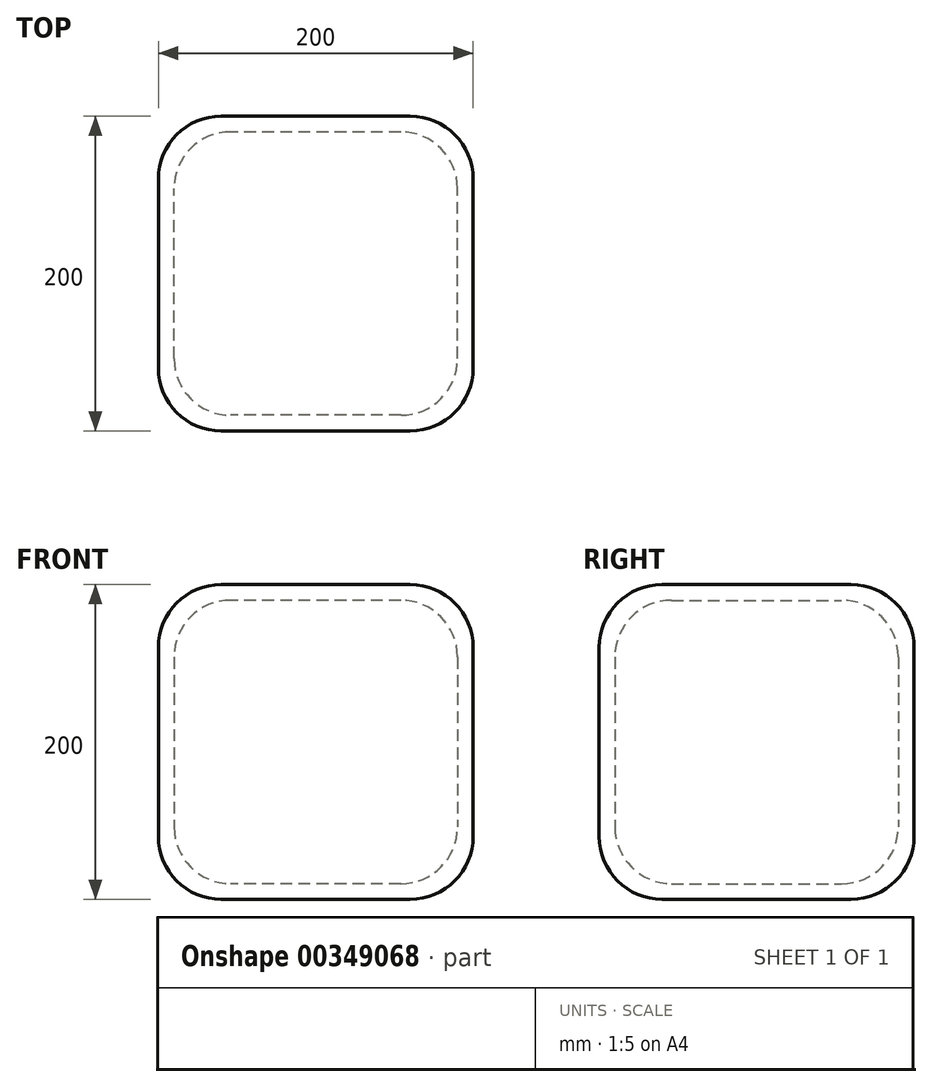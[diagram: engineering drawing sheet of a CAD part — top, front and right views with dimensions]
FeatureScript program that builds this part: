
annotation { "Feature Type Name" : "Feature", "Feature Type Description" : "" }
export const myFeature = defineFeature(function(context is Context, id is Id, definition is map)
    precondition{}
    {
        {
            var Q0;
            Q0=qCreatedBy(makeId("Top.planeOp"),FACE);
            var sketch = newSketch(context, id + "F0", { "sketchPlane" : qUnion([Q0])});
            skLineSegment(sketch, "E0.bottom", {"start": v(100, -100) * mm, "end": v(-100, -100) * mm});
            skLineSegment(sketch, "E0.top", {"start": v(100, 100) * mm, "end": v(-100, 100) * mm});
            skLineSegment(sketch, "E0.left", {"start": v(100, -100) * mm, "end": v(100, 100) * mm});
            skLineSegment(sketch, "E0.right", {"start": v(-100, -100) * mm, "end": v(-100, 100) * mm});
            skPoint(sketch, "E0.middle", {"position": v(0, 0) * mm});
            skSolve(sketch);
        }
        {
            var Q0;
            Q0 = qSketchRegion(id + "F0", true);
            extrude(context, id + "F1", {"entities" : qUnion([Q0]), "depth" : 200 * mm});
        }
        {
            var Q0;
            Q0=makeQuery(id+"F1.opExtrude","SWEPT_FACE",FACE,{"disambiguationData":[OSD([sQuery(id+"F0.wireOp",EDGE,"E0.bottom")])]});
            var Q1;
            Q1=makeQuery(id+"F1.opExtrude","SWEPT_FACE",FACE,{"disambiguationData":[OSD([sQuery(id+"F0.wireOp",EDGE,"E0.top")])]});
            var Q2;
            Q2=makeQuery(id+"F1.opExtrude","CAP_FACE",FACE,{"disambiguationData":[OSD([sQuery(id+"F0.wireOp",EDGE,"E0.bottom"),sQuery(id+"F0.wireOp",EDGE,"E0.top"),sQuery(id+"F0.wireOp",EDGE,"E0.left"),sQuery(id+"F0.wireOp",EDGE,"E0.right")])],"isStart":true});
            var Q3;
            Q3=makeQuery(id+"F1.opExtrude","SWEPT_FACE",FACE,{"disambiguationData":[OSD([sQuery(id+"F0.wireOp",EDGE,"E0.left")])]});
            var Q4;
            Q4=makeQuery(id+"F1.opExtrude","CAP_FACE",FACE,{"disambiguationData":[OSD([sQuery(id+"F0.wireOp",EDGE,"E0.bottom"),sQuery(id+"F0.wireOp",EDGE,"E0.top"),sQuery(id+"F0.wireOp",EDGE,"E0.left"),sQuery(id+"F0.wireOp",EDGE,"E0.right")])],"isStart":false});
            fillet(context, id + "F2", {"entities" : qUnion([Q0, Q1, Q2, Q3, Q4]), "radius" : 40 * mm, "tangentPropagation" : true, "allowEdgeOverflow" : false});
        }
        {
            var Q0;
            Q0=makeQuery(id+"F1.opExtrude","SWEPT_BODY",BODY,{"disambiguationData":[OSD([sQuery(id+"F0.wireOp",EDGE,"E0.bottom"),sQuery(id+"F0.wireOp",EDGE,"E0.top"),sQuery(id+"F0.wireOp",EDGE,"E0.left"),sQuery(id+"F0.wireOp",EDGE,"E0.right")])]});
            var Q1;
            Q1=qCreatedBy(makeId("Origin.pointOp"),VERTEX);
            transform(context, id + "F3", {"entities" : qUnion([Q0]), "transformType" : TransformType.SCALE_UNIFORMLY, "scale" : 0.9, "scalePoint" : qUnion([Q1]), "makeCopy" : true});
        }
        {
            var Q0;
            Q0=makeQuery(id+"F3.opPattern","COPY",BODY,{"derivedFrom":makeQuery(id+"F1.opExtrude","SWEPT_BODY",BODY,{"disambiguationData":[OSD([sQuery(id+"F0.wireOp",EDGE,"E0.bottom"),sQuery(id+"F0.wireOp",EDGE,"E0.top"),sQuery(id+"F0.wireOp",EDGE,"E0.left"),sQuery(id+"F0.wireOp",EDGE,"E0.right")])]}),"instanceName":"1"});
            transform(context, id + "F4", {"entities" : qUnion([Q0]), "transformType" : TransformType.TRANSLATION_3D, "dx" : 0 * mm, "dy" : 0 * mm, "dz" : 10 * mm, "makeCopy" : false});
        }
        {
            var Q0;
            Q0=makeQuery(id+"F3.opPattern","COPY",BODY,{"derivedFrom":makeQuery(id+"F1.opExtrude","SWEPT_BODY",BODY,{"disambiguationData":[OSD([sQuery(id+"F0.wireOp",EDGE,"E0.bottom"),sQuery(id+"F0.wireOp",EDGE,"E0.top"),sQuery(id+"F0.wireOp",EDGE,"E0.left"),sQuery(id+"F0.wireOp",EDGE,"E0.right")])]}),"instanceName":"1"});
            var Q1;
            Q1=makeQuery(id+"F1.opExtrude","SWEPT_BODY",BODY,{"disambiguationData":[OSD([sQuery(id+"F0.wireOp",EDGE,"E0.bottom"),sQuery(id+"F0.wireOp",EDGE,"E0.top"),sQuery(id+"F0.wireOp",EDGE,"E0.left"),sQuery(id+"F0.wireOp",EDGE,"E0.right")])]});
            booleanBodies(context, id + "F5", {"operationType" : BooleanOperationType.SUBTRACTION, "tools" : qUnion([Q0]), "targets" : qUnion([Q1])});
        }
    });
